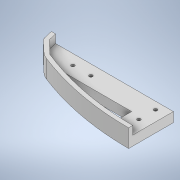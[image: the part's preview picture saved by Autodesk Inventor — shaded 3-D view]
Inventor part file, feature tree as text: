
AUTODESK INVENTOR PART (.ipt)
format: ipt  version: 2020 (Build 240168000, 168)  size: 285,184 bytes
history: native  units: mm
features: sketch x3, extrude x3, hole x2, fillet x2
ambient origin geometry x8: Origin, YZ Plane, XZ Plane, XY Plane, X Axis, Y Axis, Z Axis, Center Point
bodies: Body1 (feature_tree)
feature tree (10):
  sketch  "스케치1"
  extrude  "돌출20"  Depth=657.5mm
  extrude  "돌출21"  Depth=585.0mm
  sketch  "스케치24"
  extrude  "돌출23"  Depth=0.872665mm
  hole  "구멍5"  [1 undecoded]
  hole  "구멍6"  [1 undecoded]
  fillet  "모깎기2"  Radius=2.356194mm
  fillet  "모깎기3"  Radius=2.356194mm
  sketch  "스케치25"
note: 2 required parameter values undecoded (feature->parameter linkage not recoverable at this tier; creation-order binding heuristic only, values carry confidence <= 0.55)
